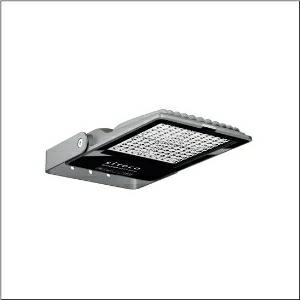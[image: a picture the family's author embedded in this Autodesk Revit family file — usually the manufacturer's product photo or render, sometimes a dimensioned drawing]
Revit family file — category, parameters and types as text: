
# Revit family: sicompact_31_mini___pl32_5xa7571c1k23_c368
name_source: partatom
category: Lighting Fixtures
units: mm (PartAtom-declared; Revit-internal decimal feet)

## family parameters
Cut with Voids When Loaded = No
Host = Face
Light Source = No
Part Type = Normal
Room Calculation Point = No
Round Connector Dimension = Use Diameter
Shared = No

## types (1)
- SiCompact 31 mini  PL32 (1 x LED, 15000 lm, 100 W, 3000K)
    Apparent Load = 100 VA
    CIE Flux Codes = 32 69 98 100 100
    Color Rendering = 70
    Color Temperature = 3000K
    Default Elevation = 1800 mm
    Description = SiCompact 31 mini, floodlight, primary light control with lens, of plastic, of toughened safety glass, transparent, light distribution: PL32, light emission: direct distribution, primary light characteristic: asymmetric, installation type: surface-mounted, LED, High Power LED, rated luminous flux: 15.000lm, luminous efficacy: 150lm/W, light colour: 730, colour temperature: 3000K, control gear: ON/OFF, with cable, 3x 1.5mm², mains connection: 220..240V, AC, 50/60Hz, connection cable pre-assembled, cable length: 2m, rated input power: 100W, of diecast aluminium, specular, metallic grey (RAL 9006), length: 461mm, width: 261mm, height: 62mm, bracket, of sheet steel, coated, metallic grey (RAL 9006), ON/OFF, protection rating (complete): IP66, insulation class (complete): insulation class I (protective earthing), certification: CE, ENEC, impact resistance: IK08, permissible operating ambient temperature: -40..+45°C, packaging unit: 1 piece

Light Distribution: PL32
    Height = 62 mm  [stored 0.203412 ft]
    Lamp = 1 x LED
    Lamp Light Flux = 15000 lm
    Lamp Power = 100 W
    Lamp count = 1
    Length = 460 mm
    Luminous efficacy = 150 lm/W
    Manufacturer = Siteco
    ModVariant = No
    Model = 5XA7571C1K23
    Mounting Place = Wall
    Mounting Type = Surface mounted
    Number of Poles = 1
    OnlyDefault = Yes
    Power Factor = 1
    Product Name = SiCompact 31 mini | PL32
    Product group = floodlight | wall mounted
    ProductGroupID = 2002
    Protection Class = Protection class I
    Protection Degree = IP 66
    RLX_Detail_Level = 1
    RLX_Emergency_Light_Flux = 0 lm
    RLX_Emergency_Type = 0
    RLX_Emergency_Type_DB = No
    RlxData = <blob elided: 126837 chars, md5=3fd24b5c>
    Socket = socket
    Standby Power = 0 W
    System Light Flux = 15000 lm
    System Power = 100 W
    Type Comments = Product without accessories
    Type Image = l_1006951.jpg
    URL = http://relux.com
    VarID = ---
    Voltage = 0 V
    Weight = 0.00 kg
    Width = 260 mm

note: [stored X ft] marks values corroborated as IEEE doubles in the binary element streams (Revit-internal decimal feet)

## geometry (parser evidence)
native form markers: Blend x4, Sweep x13
no freeform markers — native parametric forms only
